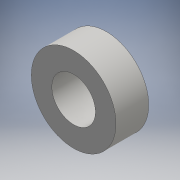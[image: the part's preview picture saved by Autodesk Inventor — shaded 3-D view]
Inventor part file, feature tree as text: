
AUTODESK INVENTOR PART (.ipt)
format: ipt  version: 2016 (Build 200138000, 138)  size: 96,256 bytes
history: native  units: mm
features: extrude x1, sketch x1
ambient origin geometry x8: Origin, YZ Plane, XZ Plane, XY Plane, X Axis, Y Axis, Z Axis, Center Point
bodies: Solid1 (feature_tree)
feature tree (2):
  extrude  "Extrusion1"  Depth=3.0mm
  sketch  "Sketch1"  dims[d0=4.0mm d1=7.77mm d2=3.0mm d3=0.0mm]
